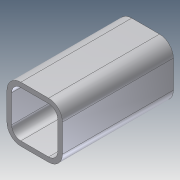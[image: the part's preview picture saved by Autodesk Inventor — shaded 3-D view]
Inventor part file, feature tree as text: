
AUTODESK INVENTOR PART (.ipt)
format: ipt  version: unknown  size: 180,224 bytes
history: native  units: in
note: dims shown in document units (in); Inventor stores cm internally (conversion verified against a paired STEP export)
features: extrude x1, sketch x1
ambient origin geometry x8: Origin, YZ Plane, XZ Plane, XY Plane, X Axis, Y Axis, Z Axis, Center Point
bodies: Solid1 (feature_tree)
feature tree (2):
  extrude  "Extrusion1"  Depth=1.5in
  sketch  "Sketch1"  dims[d0=0.375in d1=1.5in d2=0.125in d3=3.0in d4=0.0in]
